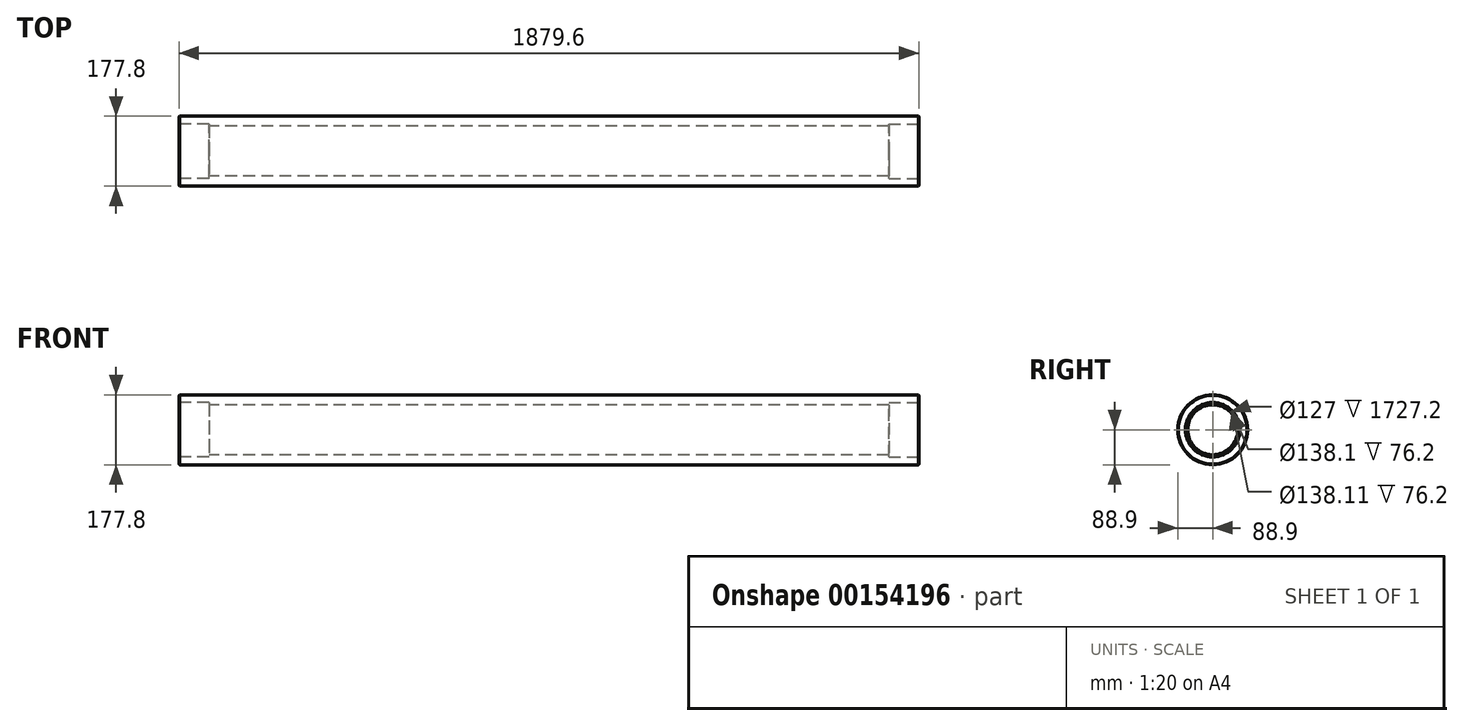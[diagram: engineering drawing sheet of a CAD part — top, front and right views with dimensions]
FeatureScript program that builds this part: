
annotation { "Feature Type Name" : "Feature", "Feature Type Description" : "" }
export const myFeature = defineFeature(function(context is Context, id is Id, definition is map)
    precondition{}
    {
        {
            var Q0;
            Q0=qCreatedBy(makeId("Right.planeOp"),FACE);
            var sketch = newSketch(context, id + "F0", { "sketchPlane" : qUnion([Q0])});
            skCircle(sketch, "E0", {"center": v(0, 0) * mm, "radius": 88.9 * mm});
            skCircle(sketch, "E1", {"center": v(0, 0) * mm, "radius": 63.5 * mm});
            skSolve(sketch);
        }
        {
            var Q0;
            Q0=qSketchRegion(id+"F0",true);
            extrude(context, id + "F1", {"entities" : qUnion([Q0]), "endBound" : BoundingType.SYMMETRIC, "depth" : 1879.6 * mm});
        }
        {
            var Q0;
            Q0=makeQuery(id+"F1.opExtrude","CAP_FACE",FACE,{"disambiguationData":[OSD([sQuery(id+"F0.wireOp",EDGE,"E0"),sQuery(id+"F0.wireOp",EDGE,"E1")])],"isStart":false});
            var sketch = newSketch(context, id + "F2", { "sketchPlane" : qUnion([Q0])});
            skCircle(sketch, "E2", {"center": v(0, 0) * mm, "radius": 69.05 * mm});
            skSolve(sketch);
        }
        {
            var Q0;
            Q0=makeQuery(id+"F2.imprint","IMPRINT",FACE,{"disambiguationData":[TD([[makeQuery(id+"F2.imprint","IMPRINT",EDGE,{"derivedFrom":sQuery(id+"F2.wireOp",EDGE,"E2")}),1.0]])]});
            extrude(context, id + "F3", {"entities" : qUnion([Q0]), "operationType" : NewBodyOperationType.REMOVE, "oppositeDirection" : true, "depth" : 76.2 * mm});
        }
        {
            var Q0;
            Q0=makeQuery(id+"F1.opExtrude","CAP_FACE",FACE,{"disambiguationData":[OSD([sQuery(id+"F0.wireOp",EDGE,"E0"),sQuery(id+"F0.wireOp",EDGE,"E1")])],"isStart":true});
            var sketch = newSketch(context, id + "F4", { "sketchPlane" : qUnion([Q0])});
            skCircle(sketch, "E3", {"center": v(0, 0) * mm, "radius": 69.06 * mm});
            skSolve(sketch);
        }
        {
            var Q0;
            Q0=qSketchRegion(id+"F4",true);
            extrude(context, id + "F5", {"entities" : qUnion([Q0]), "operationType" : NewBodyOperationType.REMOVE, "oppositeDirection" : true, "depth" : 76.2 * mm});
        }
        {
            var Q0;
            Q0=makeQuery(id+"F1.opExtrude","CAP_EDGE",EDGE,{"disambiguationData":[OSD([sQuery(id+"F0.wireOp",EDGE,"E0")])],"isStart":true});
            var Q1;
            Q1=makeQuery(id+"F1.opExtrude","CAP_EDGE",EDGE,{"disambiguationData":[OSD([sQuery(id+"F0.wireOp",EDGE,"E0")])],"isStart":false});
            chamfer(context, id + "F6", {"entities" : qUnion([Q0, Q1]), "width" : 1.52 * mm, "tangentPropagation" : true});
        }
    });
